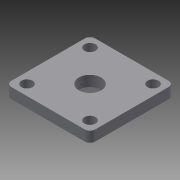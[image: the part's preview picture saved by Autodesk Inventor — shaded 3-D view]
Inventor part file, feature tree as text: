
AUTODESK INVENTOR PART (.ipt)
format: ipt  version: 2015 SP1 (Build 190203100, 203)  size: 104,448 bytes
history: native  units: in
note: dims shown in document units (in); Inventor stores cm internally (conversion verified against a paired STEP export)
features: sketch x3, hole x2, extrude x1, fillet x1
ambient origin geometry x8: Origin, YZ Plane, XZ Plane, XY Plane, X Axis, Y Axis, Z Axis, Center Point
bodies: Solid1 (feature_tree)
feature tree (7):
  extrude  "Extrusion1"  Depth=2.0in
  hole  "Hole1"  [1 undecoded]
  fillet  "Fillet1"  Radius=0.25in
  hole  "Hole2"  [1 undecoded]
  sketch  "Sketch1"  dims[d0=2.0in d1=2.0in]
  sketch  "Sketch2"  dims[d2=1.0in d3=1.0in d4=0.25in d5=0.0in]
  sketch  "Sketch3"  dims[d6=1.5in d7=1.5in d8=0.75in d9=0.75in d10=0.266in d11=0.75in d12=0.507in d13=0.25in d14=0.5635in d15=1.0in d16=0.8108in d17=0.125in d18=0.531in d19=0.75in d20=0.875in d21=0.25in d22=0.5635in d23=1.0in d24=0.8108in]
note: 2 required parameter values undecoded (feature->parameter linkage not recoverable at this tier; creation-order binding heuristic only, values carry confidence <= 0.55)
